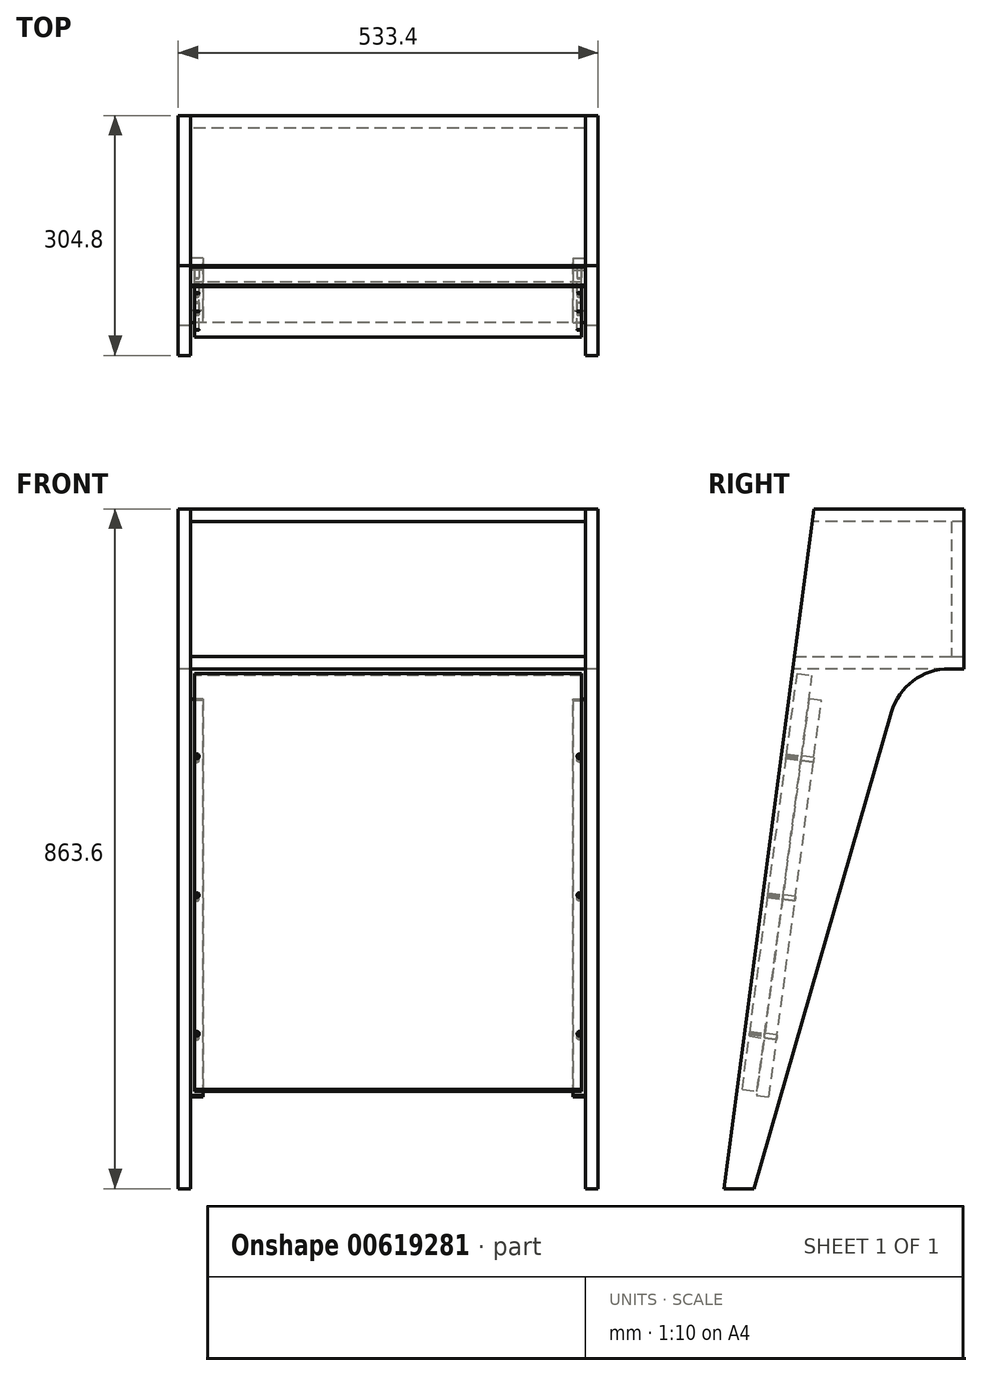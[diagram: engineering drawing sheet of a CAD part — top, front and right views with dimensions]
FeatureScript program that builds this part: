
annotation { "Feature Type Name" : "Feature", "Feature Type Description" : "" }
export const myFeature = defineFeature(function(context is Context, id is Id, definition is map)
    precondition{}
    {
        {
            var Q0;
            Q0=qCreatedBy(makeId("Right.planeOp"),FACE);
            var sketch = newSketch(context, id + "F0", { "sketchPlane" : qUnion([Q0])});
            skLineSegment(sketch, "E0", {"start": v(0, 0) * mm, "end": v(114.3, 863.6) * mm});
            skLineSegment(sketch, "E1", {"start": v(114.3, 863.6) * mm, "end": v(304.8, 863.6) * mm});
            skLineSegment(sketch, "E2", {"start": v(304.8, 863.6) * mm, "end": v(304.8, 660.4) * mm});
            skLineSegment(sketch, "E3", {"start": v(304.8, 660.4) * mm, "end": v(285.93, 660.4) * mm});
            skLineSegment(sketch, "E4", {"start": v(212.71, 605.32) * mm, "end": v(38.1, 0) * mm});
            skLineSegment(sketch, "E5", {"start": v(38.1, 0) * mm, "end": v(0, 0) * mm});
            skPoint(sketch, "E6.visualSharp", {"position": v(228.6, 660.4) * mm});
            skArc(sketch, "E6.filletArc", {"start": v(285.93, 660.4) * mm, "mid": v(240.12, 645.1) * mm, "end": v(212.71, 605.32) * mm});
            skSolve(sketch);
        }
        {
            var Q0;
            Q0 = qSketchRegion(id + "F0", true);
            extrude(context, id + "F1", {"entities" : qUnion([Q0]), "depth" : 15.88 * mm, "offsetDistance" : 25.4 * mm});
        }
        {
            var Q0;
            Q0=makeQuery(id+"F1.opExtrude","CAP_FACE",FACE,{"disambiguationData":[OSD([sQuery(id+"F0.wireOp",EDGE,"E0"),sQuery(id+"F0.wireOp",EDGE,"E1"),sQuery(id+"F0.wireOp",EDGE,"E2"),sQuery(id+"F0.wireOp",EDGE,"E3"),sQuery(id+"F0.wireOp",EDGE,"E4"),sQuery(id+"F0.wireOp",EDGE,"E5"),sQuery(id+"F0.wireOp",EDGE,"E6.filletArc")])],"isStart":false});
            var sketch = newSketch(context, id + "F2", { "sketchPlane" : qUnion([Q0])});
            skLineSegment(sketch, "E7", {"start": v(114.3, 863.6) * mm, "end": v(304.8, 863.6) * mm});
            skLineSegment(sketch, "E8", {"start": v(304.8, 863.6) * mm, "end": v(304.8, 847.73) * mm});
            skLineSegment(sketch, "E9", {"start": v(304.8, 847.73) * mm, "end": v(112.2, 847.73) * mm});
            skLineSegment(sketch, "E10", {"start": v(112.2, 847.73) * mm, "end": v(114.3, 863.6) * mm});
            skSolve(sketch);
        }
        {
            var Q0;
            Q0 = qSketchRegion(id + "F2", true);
            extrude(context, id + "F3", {"entities" : qUnion([Q0]), "depth" : 501.65 * mm, "offsetDistance" : 25.4 * mm});
        }
        {
            var Q0;
            Q0=makeQuery(id+"F1.opExtrude","CAP_FACE",FACE,{"disambiguationData":[OSD([sQuery(id+"F0.wireOp",EDGE,"E0"),sQuery(id+"F0.wireOp",EDGE,"E1"),sQuery(id+"F0.wireOp",EDGE,"E2"),sQuery(id+"F0.wireOp",EDGE,"E3"),sQuery(id+"F0.wireOp",EDGE,"E4"),sQuery(id+"F0.wireOp",EDGE,"E5"),sQuery(id+"F0.wireOp",EDGE,"E6.filletArc")])],"isStart":false});
            var sketch = newSketch(context, id + "F4", { "sketchPlane" : qUnion([Q0])});
            skLineSegment(sketch, "E11", {"start": v(304.8, 660.4) * mm, "end": v(304.8, 676.27) * mm});
            skLineSegment(sketch, "E12", {"start": v(304.8, 660.4) * mm, "end": v(87.4, 660.4) * mm});
            skLineSegment(sketch, "E13", {"start": v(87.4, 660.4) * mm, "end": v(89.5, 676.27) * mm});
            skLineSegment(sketch, "E14", {"start": v(89.5, 676.27) * mm, "end": v(304.8, 676.27) * mm});
            skSolve(sketch);
        }
        {
            var Q0;
            Q0 = qSketchRegion(id + "F4", true);
            extrude(context, id + "F5", {"entities" : qUnion([Q0]), "depth" : 501.65 * mm, "offsetDistance" : 25.4 * mm});
        }
        {
            var Q0;
            Q0=makeQuery(id+"F1.opExtrude","CAP_FACE",FACE,{"disambiguationData":[OSD([sQuery(id+"F0.wireOp",EDGE,"E0"),sQuery(id+"F0.wireOp",EDGE,"E1"),sQuery(id+"F0.wireOp",EDGE,"E2"),sQuery(id+"F0.wireOp",EDGE,"E3"),sQuery(id+"F0.wireOp",EDGE,"E4"),sQuery(id+"F0.wireOp",EDGE,"E5"),sQuery(id+"F0.wireOp",EDGE,"E6.filletArc")])],"isStart":false});
            var sketch = newSketch(context, id + "F6", { "sketchPlane" : qUnion([Q0])});
            skLineSegment(sketch, "E15", {"start": v(304.8, 676.27) * mm, "end": v(304.8, 847.73) * mm});
            skLineSegment(sketch, "E16", {"start": v(304.8, 847.73) * mm, "end": v(288.93, 847.73) * mm});
            skLineSegment(sketch, "E17", {"start": v(288.93, 847.73) * mm, "end": v(288.93, 676.27) * mm});
            skLineSegment(sketch, "E18", {"start": v(288.93, 676.27) * mm, "end": v(304.8, 676.27) * mm});
            skSolve(sketch);
        }
        {
            var Q0;
            Q0 = qSketchRegion(id + "F6", true);
            extrude(context, id + "F7", {"entities" : qUnion([Q0]), "depth" : 501.65 * mm, "offsetDistance" : 25.4 * mm});
        }
        {
            var Q0;
            Q0=makeQuery(id+"F5.opExtrude","CAP_FACE",FACE,{"disambiguationData":[OSD([sQuery(id+"F4.wireOp",EDGE,"E11"),sQuery(id+"F4.wireOp",EDGE,"E12"),sQuery(id+"F4.wireOp",EDGE,"E13"),sQuery(id+"F4.wireOp",EDGE,"E14")])],"isStart":false});
            var sketch = newSketch(context, id + "F8", { "sketchPlane" : qUnion([Q0])});
            skLineSegment(sketch, "E19.0", {"start": v(0, 0) * mm, "end": v(114.3, 863.6) * mm});
            skLineSegment(sketch, "E20.0", {"start": v(304.8, 847.73) * mm, "end": v(304.8, 676.27) * mm});
            skArc(sketch, "E21.0", {"start": v(285.93, 660.4) * mm, "mid": v(240.12, 645.1) * mm, "end": v(212.71, 605.32) * mm});
            skPoint(sketch, "E22.0", {"position": v(304.8, 668.34) * mm});
            skLineSegment(sketch, "E23.0", {"start": v(212.71, 605.32) * mm, "end": v(38.1, 0) * mm});
            skLineSegment(sketch, "E24.0", {"start": v(38.1, 0) * mm, "end": v(0, 0) * mm});
            skLineSegment(sketch, "E25.1", {"start": v(304.8, 863.6) * mm, "end": v(304.8, 847.73) * mm});
            skPoint(sketch, "E25.2", {"position": v(304.8, 855.66) * mm});
            skLineSegment(sketch, "E26.0", {"start": v(114.3, 863.6) * mm, "end": v(304.8, 863.6) * mm});
            skLineSegment(sketch, "E27.0", {"start": v(304.8, 676.27) * mm, "end": v(304.8, 660.4) * mm});
            skLineSegment(sketch, "E28", {"start": v(304.8, 660.4) * mm, "end": v(285.93, 660.4) * mm});
            skSolve(sketch);
        }
        {
            var Q0;
            Q0 = qSketchRegion(id + "F8", true);
            extrude(context, id + "F9", {"entities" : qUnion([Q0]), "depth" : 15.88 * mm, "offsetDistance" : 25.4 * mm});
        }
        {
            var Q0;
            Q0=makeQuery(id+"F1.opExtrude","CAP_FACE",FACE,{"disambiguationData":[OSD([sQuery(id+"F0.wireOp",EDGE,"E0"),sQuery(id+"F0.wireOp",EDGE,"E1"),sQuery(id+"F0.wireOp",EDGE,"E2"),sQuery(id+"F0.wireOp",EDGE,"E3"),sQuery(id+"F0.wireOp",EDGE,"E4"),sQuery(id+"F0.wireOp",EDGE,"E5"),sQuery(id+"F0.wireOp",EDGE,"E6.filletArc")])],"isStart":false});
            var sketch = newSketch(context, id + "F10", { "sketchPlane" : qUnion([Q0])});
            skLineSegment(sketch, "E29", {"start": v(107.98, 622.3) * mm, "end": v(41.33, 118.7) * mm});
            skLineSegment(sketch, "E30", {"start": v(41.33, 118.7) * mm, "end": v(57.07, 116.6) * mm});
            skLineSegment(sketch, "E31", {"start": v(57.07, 116.6) * mm, "end": v(123.72, 620.22) * mm});
            skLineSegment(sketch, "E32", {"start": v(123.72, 620.22) * mm, "end": v(107.98, 622.3) * mm});
            skSolve(sketch);
        }
        {
            var Q0;
            Q0 = qSketchRegion(id + "F10", true);
            extrude(context, id + "F11", {"entities" : qUnion([Q0]), "depth" : 15.88 * mm, "offsetDistance" : 25.4 * mm});
        }
        {
            var Q0;
            Q0=makeQuery(id+"F9.opExtrude","CAP_FACE",FACE,{"disambiguationData":[OSD([sQuery(id+"F8.wireOp",EDGE,"E19.0"),sQuery(id+"F8.wireOp",EDGE,"E20.0"),sQuery(id+"F8.wireOp",EDGE,"E21.0"),sQuery(id+"F8.wireOp",EDGE,"E23.0"),sQuery(id+"F8.wireOp",EDGE,"E24.0"),sQuery(id+"F8.wireOp",EDGE,"E25.1"),sQuery(id+"F8.wireOp",EDGE,"E26.0"),sQuery(id+"F8.wireOp",EDGE,"E27.0"),sQuery(id+"F8.wireOp",EDGE,"E28")])],"isStart":true});
            var sketch = newSketch(context, id + "F12", { "sketchPlane" : qUnion([Q0])});
            skLineSegment(sketch, "E33.0", {"start": v(-107.98, 622.3) * mm, "end": v(-41.33, 118.7) * mm});
            skLineSegment(sketch, "E34.0", {"start": v(-123.72, 620.22) * mm, "end": v(-107.98, 622.3) * mm});
            skLineSegment(sketch, "E35.0", {"start": v(-57.07, 116.6) * mm, "end": v(-123.72, 620.22) * mm});
            skLineSegment(sketch, "E36.0", {"start": v(-41.33, 118.7) * mm, "end": v(-57.07, 116.6) * mm});
            skSolve(sketch);
        }
        {
            var Q0;
            Q0 = qSketchRegion(id + "F12", true);
            extrude(context, id + "F13", {"entities" : qUnion([Q0]), "depth" : 15.88 * mm, "offsetDistance" : 25.4 * mm});
        }
        {
            var Q0;
            Q0=makeQuery(id+"F11.opExtrude","SWEPT_FACE",FACE,{"disambiguationData":[OSD([sQuery(id+"F10.wireOp",EDGE,"E29")])]});
            var sketch = newSketch(context, id + "F14", { "sketchPlane" : qUnion([Q0])});
            skCircle(sketch, "E37", {"center": v(23.81, 554.89) * mm, "radius": 3 * mm});
            skCircle(sketch, "E38", {"center": v(23.81, 377.09) * mm, "radius": 3 * mm});
            skCircle(sketch, "E39", {"center": v(23.81, 199.29) * mm, "radius": 3 * mm});
            skCircle(sketch, "E40", {"center": v(509.59, 554.89) * mm, "radius": 3 * mm});
            skCircle(sketch, "E41", {"center": v(509.59, 377.09) * mm, "radius": 3 * mm});
            skCircle(sketch, "E42", {"center": v(509.59, 199.29) * mm, "radius": 3 * mm});
            skSolve(sketch);
        }
        {
            var Q0;
            Q0 = qSketchRegion(id + "F14", true);
            extrude(context, id + "F15", {"entities" : qUnion([Q0]), "operationType" : NewBodyOperationType.REMOVE, "oppositeDirection" : true, "depth" : 25.4 * mm, "offsetDistance" : 25.4 * mm});
        }
        {
            var Q0;
            Q0=makeQuery(id+"F11.opExtrude","SWEPT_FACE",FACE,{"disambiguationData":[OSD([sQuery(id+"F10.wireOp",EDGE,"E29")])]});
            var sketch = newSketch(context, id + "F16", { "sketchPlane" : qUnion([Q0])});
            skLineSegment(sketch, "E43.0", {"start": v(15.88, 123.09) * mm, "end": v(15.88, 666.16) * mm});
            skLineSegment(sketch, "E44.0", {"start": v(517.52, 666.16) * mm, "end": v(15.87, 666.16) * mm});
            skLineSegment(sketch, "E45.0", {"start": v(517.52, 123.09) * mm, "end": v(517.52, 666.16) * mm});
            skLineSegment(sketch, "E46", {"start": v(15.88, 123.09) * mm, "end": v(517.52, 123.09) * mm});
            skLineSegment(sketch, "E47.0", {"start": v(20.96, 128.17) * mm, "end": v(512.45, 128.17) * mm});
            skLineSegment(sketch, "E47.1", {"start": v(20.96, 128.17) * mm, "end": v(20.96, 661.08) * mm});
            skLineSegment(sketch, "E47.2", {"start": v(512.45, 661.08) * mm, "end": v(20.96, 661.08) * mm});
            skLineSegment(sketch, "E47.3", {"start": v(512.45, 128.17) * mm, "end": v(512.45, 661.08) * mm});
            skCircle(sketch, "E48.0", {"center": v(23.81, 199.29) * mm, "radius": 3 * mm});
            skCircle(sketch, "E48.1", {"center": v(23.81, 554.89) * mm, "radius": 3 * mm});
            skCircle(sketch, "E48.2", {"center": v(23.81, 377.09) * mm, "radius": 3 * mm});
            skCircle(sketch, "E49.0", {"center": v(509.59, 554.89) * mm, "radius": 3 * mm});
            skCircle(sketch, "E49.1", {"center": v(509.59, 377.09) * mm, "radius": 3 * mm});
            skCircle(sketch, "E49.2", {"center": v(509.59, 199.29) * mm, "radius": 3 * mm});
            skSolve(sketch);
        }
        {
            var Q0;
            {var subQ1=sQuery(id+"F16.wireOp",EDGE,"E47.2");Q0=makeQuery(id+"F16.imprint","IMPRINT",FACE,{"disambiguationData":[TD([[makeQuery(id+"F16.imprint","IMPRINT",EDGE,{"derivedFrom":subQ1}),1.0]])]});}
            var Q1;
            Q1=makeQuery(id+"F16.imprint","IMPRINT",FACE,{"disambiguationData":[TD([[makeQuery(id+"F16.imprint","IMPRINT",EDGE,{"derivedFrom":sQuery(id+"F16.wireOp",EDGE,"E48.0")}),-1.0]])]});
            extrude(context, id + "F17", {"entities" : qUnion([Q0, Q1]), "depth" : 19.05 * mm, "offsetDistance" : 25.4 * mm});
        }
    });
